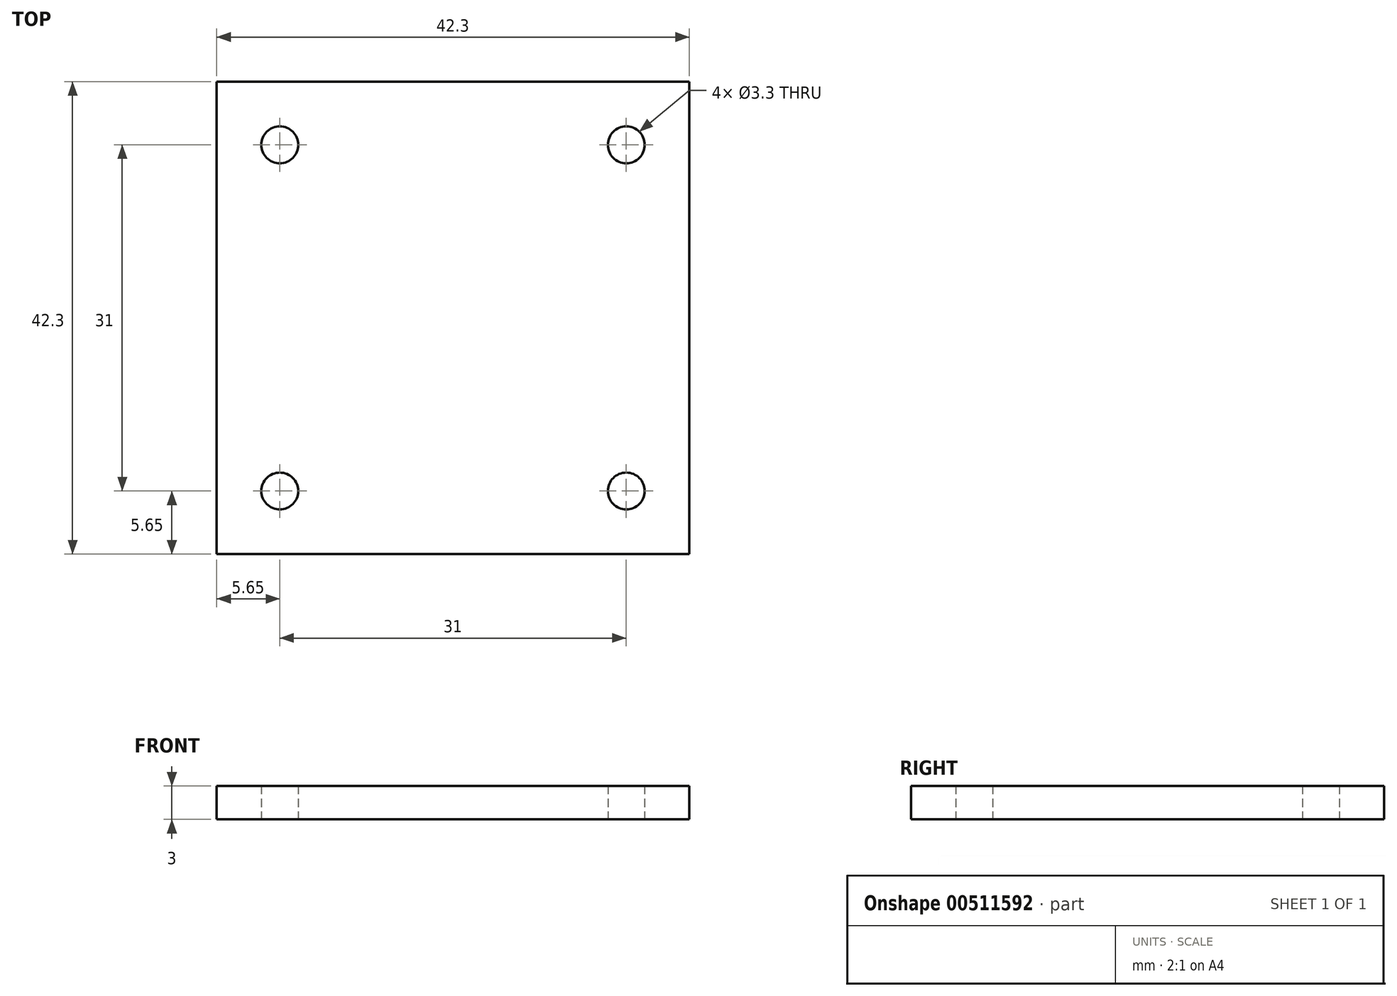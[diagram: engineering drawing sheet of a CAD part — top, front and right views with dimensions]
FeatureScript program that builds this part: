
annotation { "Feature Type Name" : "Feature", "Feature Type Description" : "" }
export const myFeature = defineFeature(function(context is Context, id is Id, definition is map)
    precondition{}
    {
        {
            var Q0;
            Q0=qCreatedBy(makeId("Top.planeOp"),FACE);
            var sketch = newSketch(context, id + "F0", { "sketchPlane" : qUnion([Q0])});
            skLineSegment(sketch, "E0.bottom", {"start": v(-21.15, -21.15) * mm, "end": v(21.15, -21.15) * mm});
            skLineSegment(sketch, "E0.top", {"start": v(-21.15, 21.15) * mm, "end": v(21.15, 21.15) * mm});
            skLineSegment(sketch, "E0.left", {"start": v(-21.15, -21.15) * mm, "end": v(-21.15, 21.15) * mm});
            skLineSegment(sketch, "E0.right", {"start": v(21.15, -21.15) * mm, "end": v(21.15, 21.15) * mm});
            skPoint(sketch, "E0.middle", {"position": v(0, 0) * mm});
            skPoint(sketch, "E1", {"position": v(-15.5, 15.5) * mm});
            skPoint(sketch, "E2", {"position": v(15.5, 15.5) * mm});
            skPoint(sketch, "E3", {"position": v(15.5, -15.5) * mm});
            skPoint(sketch, "E4", {"position": v(-15.5, -15.5) * mm});
            skSolve(sketch);
        }
        {
            var Q0;
            Q0=makeQuery(id+"F0.imprint","IMPRINT",FACE,{"disambiguationData":[TD([[makeQuery(id+"F0.imprint","IMPRINT",EDGE,{"derivedFrom":sQuery(id+"F0.wireOp",EDGE,"E0.bottom")}),1.0]])]});
            extrude(context, id + "F1", {"entities" : qUnion([Q0]), "depth" : 3 * mm});
        }
        {
            var Q0;
            Q0=sQuery(id+"F0.wireOp",VERTEX,"E3");
            var Q1;
            Q1=sQuery(id+"F0.wireOp",VERTEX,"E2");
            var Q2;
            Q2=sQuery(id+"F0.wireOp",VERTEX,"E1");
            var Q3;
            Q3=sQuery(id+"F0.wireOp",VERTEX,"E4");
            var Q4;
            Q4=makeQuery(id+"F1.opExtrude","SWEPT_BODY",BODY,{"disambiguationData":[OSD([sQuery(id+"F0.wireOp",EDGE,"E0.bottom"),sQuery(id+"F0.wireOp",EDGE,"E0.top"),sQuery(id+"F0.wireOp",EDGE,"E0.left"),sQuery(id+"F0.wireOp",EDGE,"E0.right")])]});
            hole(context, id + "F2", {"style" : HoleStyle.SIMPLE, "endStyle" : HoleEndStyle.THROUGH, "oppositeDirection" : true, "standardTappedOrClearance" : lookupTablePath({ "standard" : "ISO", "fit" : "Normal", "size" : "M3", "type" : "Clearance" }), "standardBlindInLast" : lookupTablePath({ "fit" : "Standard", "standard" : "ISO", "size" : "M3", "type" : "Clearance" }), "holeDiameter" : 3.3 * mm, "isTappedThrough" : true, "tappedDepth" : 12 * mm, "tapClearance" : 3, "locations" : qUnion([Q0, Q1, Q2, Q3]), "scope" : qUnion([Q4])});
        }
    });
